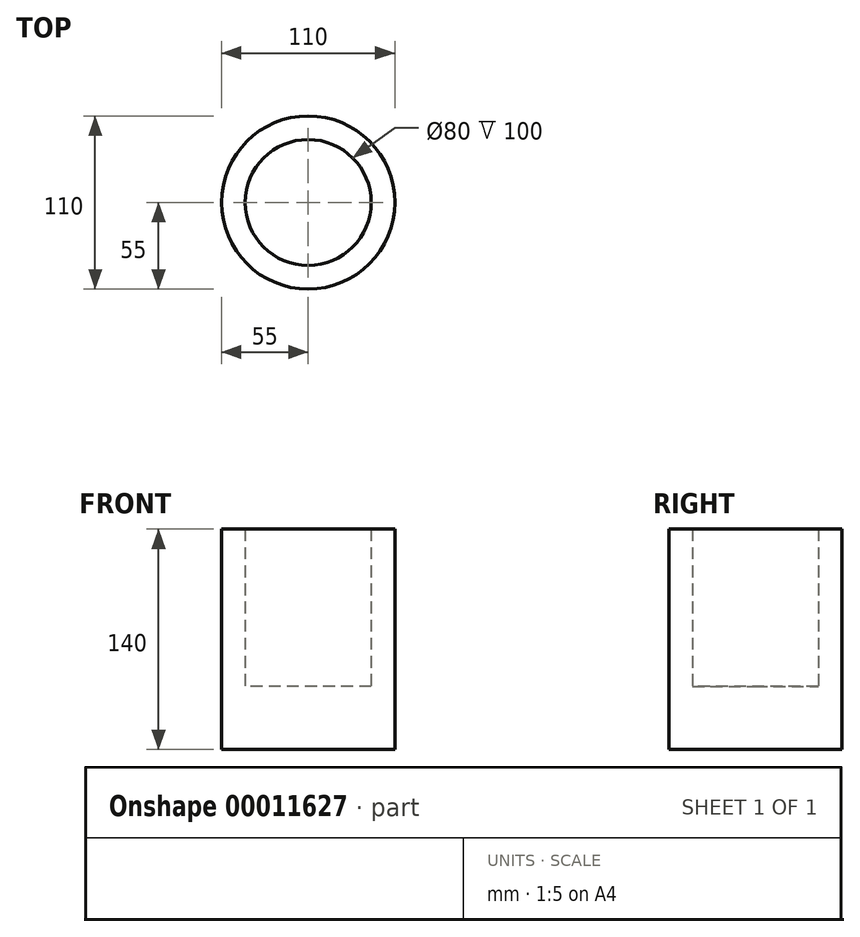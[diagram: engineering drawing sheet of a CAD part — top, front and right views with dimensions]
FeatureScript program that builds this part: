
annotation { "Feature Type Name" : "Feature", "Feature Type Description" : "" }
export const myFeature = defineFeature(function(context is Context, id is Id, definition is map)
    precondition{}
    {
        {
            var Q0;
            Q0=qCreatedBy(makeId("Top.planeOp"),FACE);
            var sketch = newSketch(context, id + "F0", { "sketchPlane" : qUnion([Q0])});
            skCircle(sketch, "E0", {"center": v(0, 0) * mm, "radius": 55 * mm});
            skCircle(sketch, "E1", {"center": v(0, 0) * mm, "radius": 40 * mm});
            skSolve(sketch);
        }
        {
            var Q0;
            Q0=makeQuery(id+"F0.imprint","IMPRINT",FACE,{"disambiguationData":[TD([[makeQuery(id+"F0.imprint","IMPRINT",EDGE,{"derivedFrom":sQuery(id+"F0.wireOp",EDGE,"E0")}),1.0]])]});
            extrude(context, id + "F1", {"entities" : qUnion([Q0]), "depth" : 100 * mm});
        }
        {
            var Q0;
            Q0=makeQuery(id+"F0.imprint","IMPRINT",FACE,{"disambiguationData":[TD([[makeQuery(id+"F0.imprint","IMPRINT",EDGE,{"derivedFrom":sQuery(id+"F0.wireOp",EDGE,"E1")}),1.0]])]});
            var Q1;
            Q1=makeQuery(id+"F0.imprint","IMPRINT",FACE,{"disambiguationData":[TD([[makeQuery(id+"F0.imprint","IMPRINT",EDGE,{"derivedFrom":sQuery(id+"F0.wireOp",EDGE,"E0")}),1.0]])]});
            extrude(context, id + "F2", {"entities" : qUnion([Q0, Q1]), "operationType" : NewBodyOperationType.ADD, "oppositeDirection" : true, "depth" : 40 * mm});
        }
    });
